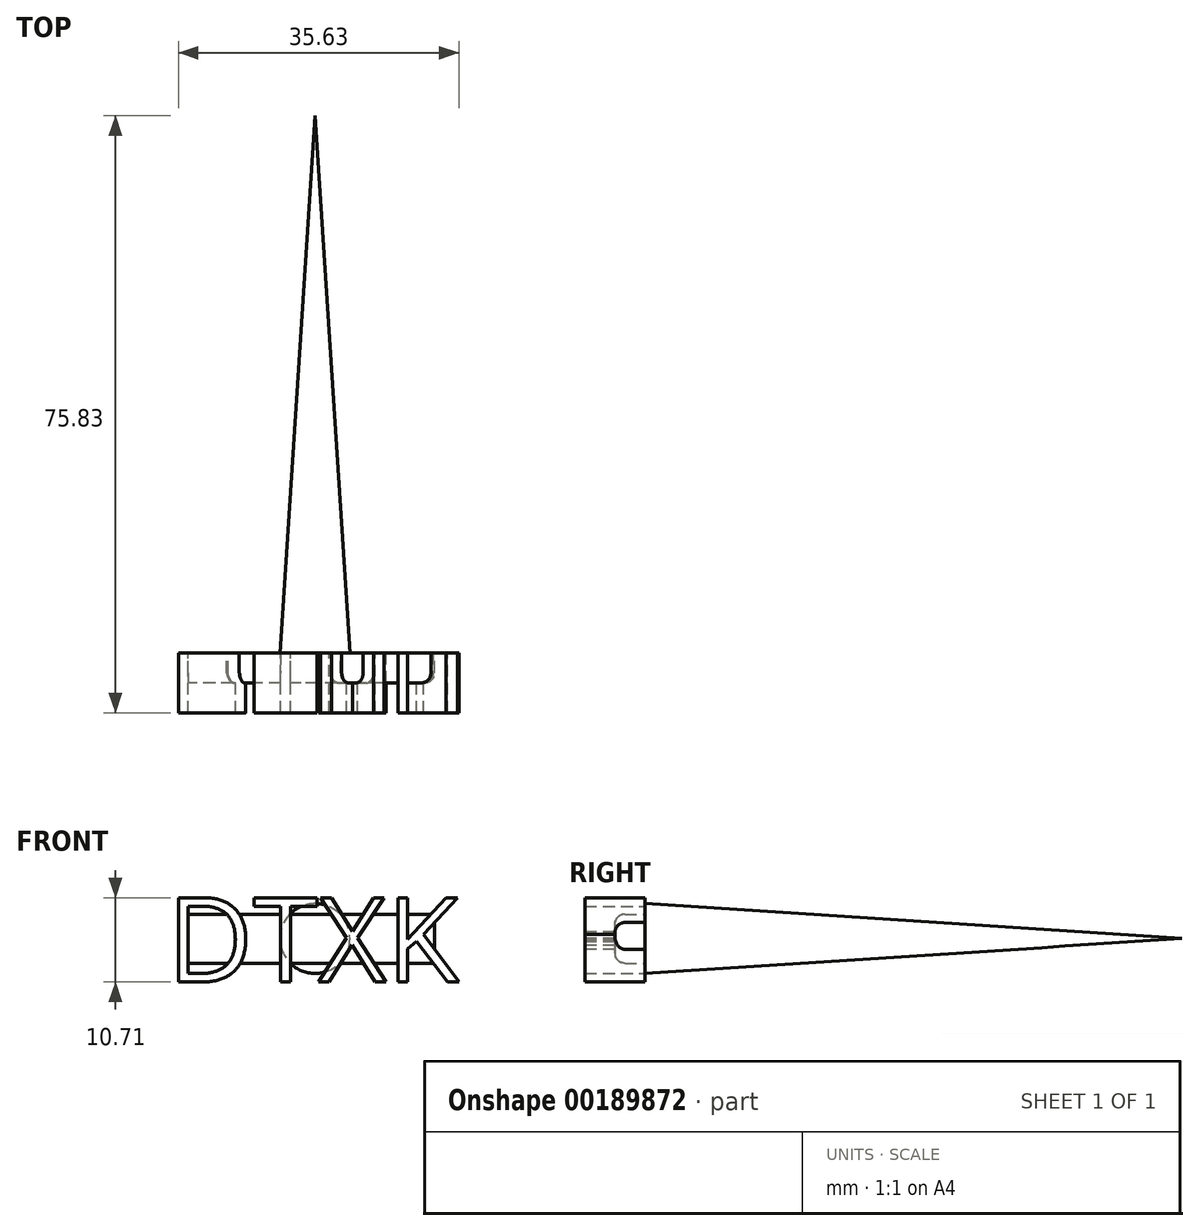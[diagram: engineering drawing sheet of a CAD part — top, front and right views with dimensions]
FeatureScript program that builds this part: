
annotation { "Feature Type Name" : "Feature", "Feature Type Description" : "" }
export const myFeature = defineFeature(function(context is Context, id is Id, definition is map)
    precondition{}
    {
        {
            var Q0;
            Q0=qCreatedBy(makeId("Front.planeOp"),FACE);
            var sketch = newSketch(context, id + "F0", { "sketchPlane" : qUnion([Q0])});
            skText(sketch, "E0", { "text": "DTXK", "fontName": "OpenSans-Regular.ttf"});
            const initialGuessF0  = {"E0": [-0.01882, -0.00553, 1, 0, 0.0108]};
            skSetInitialGuess(sketch, initialGuessF0);
            skSolve(sketch);
        }
        {
            var Q0;
            Q0 = qSketchRegion(id + "F0", true);
            extrude(context, id + "F1", {"entities" : qUnion([Q0]), "depth" : 7.62 * mm});
        }
        {
            var Q0;
            Q0=qCreatedBy(makeId("Front.planeOp"),FACE);
            var sketch = newSketch(context, id + "F2", { "sketchPlane" : qUnion([Q0])});
            skLineSegment(sketch, "E1.bottom", {"start": v(15.21, 3.09) * mm, "end": v(-16.9, 3.09) * mm});
            skLineSegment(sketch, "E1.top", {"start": v(15.21, -3.14) * mm, "end": v(-16.9, -3.14) * mm});
            skLineSegment(sketch, "E1.left", {"start": v(15.21, 3.09) * mm, "end": v(15.21, -3.14) * mm});
            skLineSegment(sketch, "E1.right", {"start": v(-16.9, 3.09) * mm, "end": v(-16.9, -3.14) * mm});
            skSolve(sketch);
        }
        {
            var Q0;
            Q0=makeQuery(id+"F2.imprint","IMPRINT",FACE,{"disambiguationData":[TD([[makeQuery(id+"F2.imprint","IMPRINT",EDGE,{"derivedFrom":sQuery(id+"F2.wireOp",EDGE,"E1.bottom")}),1.0]])]});
            extrude(context, id + "F3", {"entities" : qUnion([Q0]), "operationType" : NewBodyOperationType.ADD, "depth" : 3.8 * mm});
        }
        {
            var Q0;
            Q0=qCreatedBy(makeId("Top.planeOp"),FACE);
            var sketch = newSketch(context, id + "F4", { "sketchPlane" : qUnion([Q0])});
            skLineSegment(sketch, "E2", {"start": v(0, 0) * mm, "end": v(0, 68.21) * mm});
            skLineSegment(sketch, "E3", {"start": v(0, 68.21) * mm, "end": v(-4.44, 0) * mm});
            skLineSegment(sketch, "E4", {"start": v(-4.44, 0) * mm, "end": v(0, 0) * mm});
            skSolve(sketch);
        }
        {
            var Q0;
            Q0 = qSketchRegion(id + "F4", true);
            var Q1;
            Q1=sQuery(id+"F4.wireOp",EDGE,"E2");
            revolve(context, id + "F5", {"entities" : qUnion([Q0]), "axis" : qUnion([Q1]), "revolveType" : RevolveType.FULL});
        }
        {
            var Q0;
            Q0=makeQuery(id+"F3.opExtrude","CAP_EDGE",EDGE,{"disambiguationData":[OSD([sQuery(id+"F2.wireOp",EDGE,"E1.bottom")])],"isStart":false});
            var Q1;
            Q1=makeQuery(id+"F3.opExtrude","CAP_EDGE",EDGE,{"disambiguationData":[OSD([sQuery(id+"F2.wireOp",EDGE,"E1.top")])],"isStart":false});
            var Q2;
            Q2=makeQuery(id+"F3.opExtrude","CAP_EDGE",EDGE,{"disambiguationData":[OSD([sQuery(id+"F2.wireOp",EDGE,"E1.right")])],"isStart":false});
            var Q3;
            Q3=makeQuery(id+"F3.opExtrude","CAP_EDGE",EDGE,{"disambiguationData":[OSD([sQuery(id+"F2.wireOp",EDGE,"E1.left")])],"isStart":false});
            fillet(context, id + "F6", {"entities" : qUnion([Q0, Q1, Q2, Q3]), "radius" : 1.27 * mm, "tangentPropagation" : true, "allowEdgeOverflow" : false});
        }
    });
